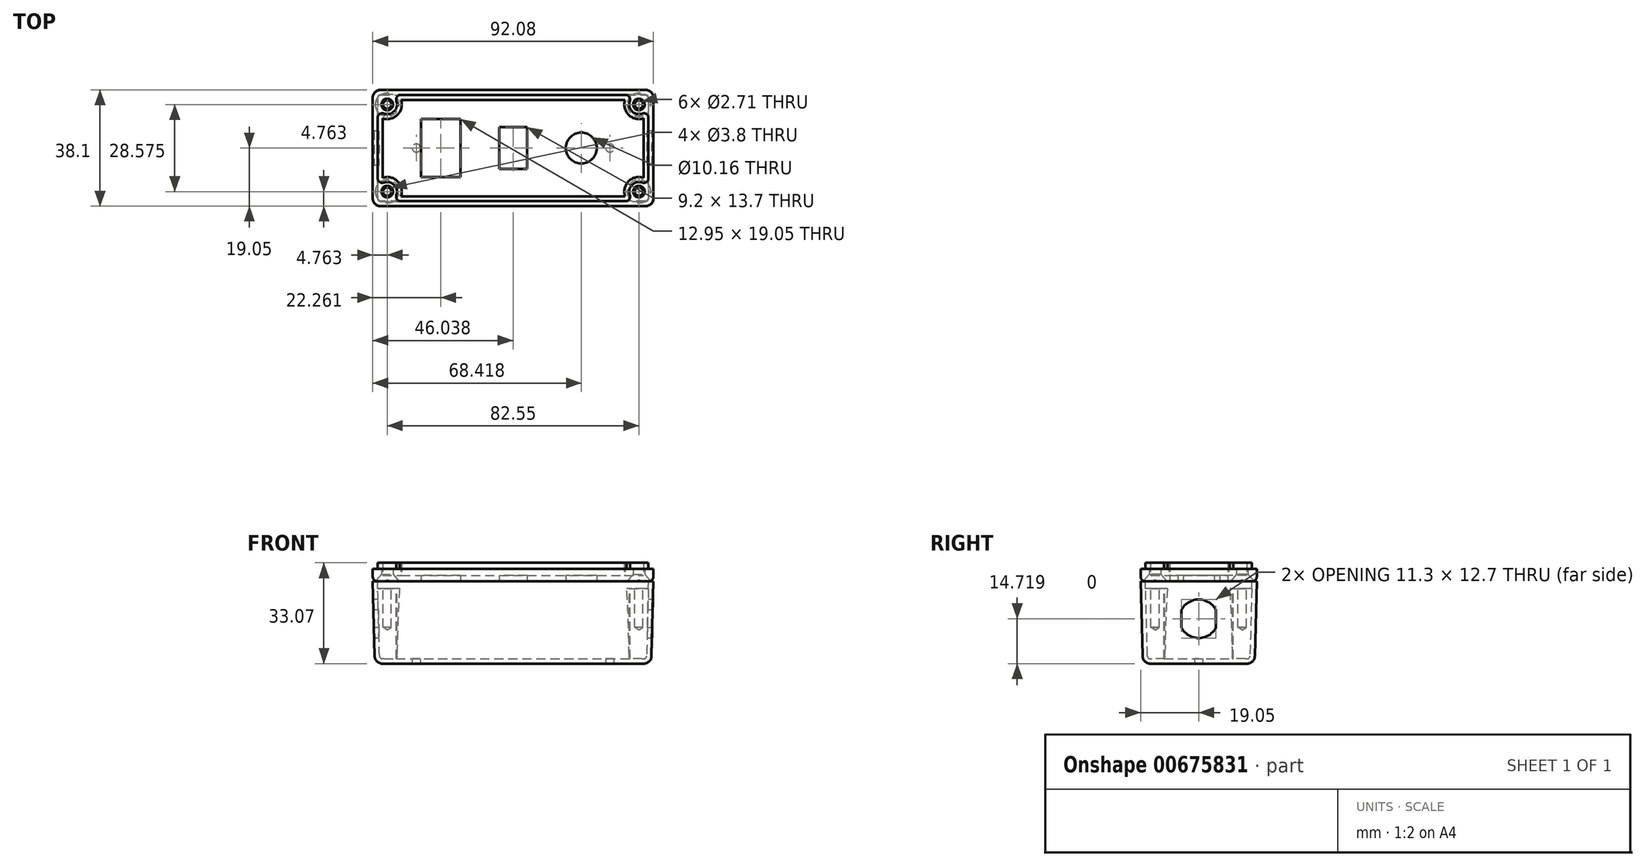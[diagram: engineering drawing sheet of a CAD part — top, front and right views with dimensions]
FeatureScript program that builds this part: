
annotation { "Feature Type Name" : "Feature", "Feature Type Description" : "" }
export const myFeature = defineFeature(function(context is Context, id is Id, definition is map)
    precondition{}
    {
        {
            var Q0;
            Q0=qCreatedBy(makeId("Top.planeOp"),FACE);
            var sketch = newSketch(context, id + "F0", { "sketchPlane" : qUnion([Q0])});
            skLineSegment(sketch, "E0.bottom", {"start": v(0, 0) * mm, "end": v(92.07, 0) * mm});
            skLineSegment(sketch, "E0.top", {"start": v(0, 38.1) * mm, "end": v(92.07, 38.1) * mm});
            skLineSegment(sketch, "E0.left", {"start": v(0, 0) * mm, "end": v(0, 38.1) * mm});
            skLineSegment(sketch, "E0.right", {"start": v(92.07, 0) * mm, "end": v(92.07, 38.1) * mm});
            skSolve(sketch);
        }
        {
            var Q0;
            Q0 = qSketchRegion(id + "F0", true);
            extrude(context, id + "F1", {"entities" : qUnion([Q0]), "oppositeDirection" : true, "depth" : 26.97 * mm, "offsetDistance" : 25.4 * mm, "hasDraft" : true, "draftAngle" : 1.5 * degree, "draftPullDirection" : true});
        }
        {
            var Q0;
            Q0=makeQuery(id+"F1.opExtrude","SWEPT_EDGE",EDGE,{"disambiguationData":[OSD([sQuery(id+"F0.wireOp",EDGE,"E0.bottom"),sQuery(id+"F0.wireOp",EDGE,"E0.right")])]});
            var Q1;
            Q1=makeQuery(id+"F1.opExtrude","CAP_EDGE",EDGE,{"disambiguationData":[OSD([sQuery(id+"F0.wireOp",EDGE,"E0.bottom")])],"isStart":false});
            var Q2;
            Q2=makeQuery(id+"F1.opExtrude","SWEPT_EDGE",EDGE,{"disambiguationData":[OSD([sQuery(id+"F0.wireOp",EDGE,"E0.bottom"),sQuery(id+"F0.wireOp",EDGE,"E0.left")])]});
            var Q3;
            Q3=makeQuery(id+"F1.opExtrude","SWEPT_EDGE",EDGE,{"disambiguationData":[OSD([sQuery(id+"F0.wireOp",EDGE,"E0.top"),sQuery(id+"F0.wireOp",EDGE,"E0.left")])]});
            var Q4;
            Q4=makeQuery(id+"F1.opExtrude","CAP_EDGE",EDGE,{"disambiguationData":[OSD([sQuery(id+"F0.wireOp",EDGE,"E0.left")])],"isStart":false});
            var Q5;
            Q5=makeQuery(id+"F1.opExtrude","CAP_EDGE",EDGE,{"disambiguationData":[OSD([sQuery(id+"F0.wireOp",EDGE,"E0.right")])],"isStart":false});
            var Q6;
            Q6=makeQuery(id+"F1.opExtrude","SWEPT_EDGE",EDGE,{"disambiguationData":[OSD([sQuery(id+"F0.wireOp",EDGE,"E0.top"),sQuery(id+"F0.wireOp",EDGE,"E0.right")])]});
            var Q7;
            Q7=makeQuery(id+"F1.opExtrude","CAP_EDGE",EDGE,{"disambiguationData":[OSD([sQuery(id+"F0.wireOp",EDGE,"E0.top")])],"isStart":false});
            fillet(context, id + "F2", {"entities" : qUnion([Q0, Q1, Q2, Q3, Q4, Q5, Q6, Q7]), "radius" : 2.54 * mm, "tangentPropagation" : true, "allowEdgeOverflow" : false});
        }
        {
            var Q0;
            Q0=makeQuery(id+"F1.opExtrude","CAP_FACE",FACE,{"disambiguationData":[OSD([sQuery(id+"F0.wireOp",EDGE,"E0.bottom"),sQuery(id+"F0.wireOp",EDGE,"E0.top"),sQuery(id+"F0.wireOp",EDGE,"E0.left"),sQuery(id+"F0.wireOp",EDGE,"E0.right")])],"isStart":true});
            shell(context, id + "F3", {"entities" : qUnion([Q0]), "thickness" : 1.57 * mm});
        }
        {
            var Q0;
            Q0=makeQuery(id+"F1.opExtrude","CAP_FACE",FACE,{"disambiguationData":[OSD([sQuery(id+"F0.wireOp",EDGE,"E0.bottom"),sQuery(id+"F0.wireOp",EDGE,"E0.top"),sQuery(id+"F0.wireOp",EDGE,"E0.left"),sQuery(id+"F0.wireOp",EDGE,"E0.right")])],"isStart":true});
            cPlane(context, id + "F4", {"entities" : qUnion([Q0]), "cplaneType" : CPlaneType.OFFSET, "offset" : 2.4 * mm, "oppositeDirection" : true, "width" : 152.4 * mm, "height" : 152.4 * mm});
        }
        {
            var Q0;
            Q0=qCreatedBy(id+"F4.planeOp",FACE);
            var sketch = newSketch(context, id + "F5", { "sketchPlane" : qUnion([Q0])});
            skArc(sketch, "E1", {"start": v(3.68, 30.35) * mm, "mid": v(7, 31.1) * mm, "end": v(7.75, 34.42) * mm});
            skLineSegment(sketch, "E2", {"start": v(46.04, 38.1) * mm, "end": v(46.04, 0) * mm, "construction": true});
            skLineSegment(sketch, "E3", {"start": v(0, 19.05) * mm, "end": v(92.08, 19.05) * mm, "construction": true});
            skPoint(sketch, "E3.endSnap0", {"position": v(46.04, 19.05) * mm});
            skArc(sketch, "E4", {"start": v(9.23, 36.52) * mm, "mid": v(7.94, 35.85) * mm, "end": v(7.75, 34.42) * mm});
            skArc(sketch, "E5", {"start": v(3.68, 30.35) * mm, "mid": v(2.25, 30.16) * mm, "end": v(1.58, 28.87) * mm});
            skLineSegment(sketch, "E6", {"start": v(1.58, 28.87) * mm, "end": v(1.58, 36.52) * mm});
            skLineSegment(sketch, "E7", {"start": v(1.58, 36.52) * mm, "end": v(9.23, 36.52) * mm});
            skPoint(sketch, "E8", {"position": v(4.76, 4.76) * mm});
            skPoint(sketch, "E9", {"position": v(87.31, 4.76) * mm});
            skPoint(sketch, "E10", {"position": v(87.31, 33.34) * mm});
            skLineSegment(sketch, "E11.MirrorCS", {"start": v(90.5, 36.52) * mm, "end": v(82.84, 36.52) * mm});
            skArc(sketch, "E12.MirrorCS", {"start": v(82.84, 36.52) * mm, "mid": v(84.13, 35.85) * mm, "end": v(84.33, 34.42) * mm});
            skArc(sketch, "E13.MirrorCS", {"start": v(88.4, 30.35) * mm, "mid": v(85.07, 31.1) * mm, "end": v(84.33, 34.42) * mm});
            skArc(sketch, "E14.MirrorCS", {"start": v(88.4, 30.35) * mm, "mid": v(89.83, 30.16) * mm, "end": v(90.5, 28.87) * mm});
            skLineSegment(sketch, "E15.MirrorCS", {"start": v(90.5, 28.87) * mm, "end": v(90.5, 36.52) * mm});
            skArc(sketch, "E16.MirrorCS", {"start": v(3.68, 7.75) * mm, "mid": v(7, 7) * mm, "end": v(7.75, 3.68) * mm});
            skArc(sketch, "E17.MirrorCS", {"start": v(3.68, 7.75) * mm, "mid": v(2.25, 7.94) * mm, "end": v(1.58, 9.23) * mm});
            skLineSegment(sketch, "E18.MirrorCS", {"start": v(1.58, 9.23) * mm, "end": v(1.58, 1.58) * mm});
            skLineSegment(sketch, "E19.MirrorCS", {"start": v(1.58, 1.58) * mm, "end": v(9.23, 1.58) * mm});
            skArc(sketch, "E20.MirrorCS", {"start": v(9.23, 1.58) * mm, "mid": v(7.94, 2.25) * mm, "end": v(7.75, 3.68) * mm});
            skLineSegment(sketch, "E21.MirrorCS", {"start": v(90.5, 9.23) * mm, "end": v(90.5, 1.58) * mm});
            skArc(sketch, "E22.MirrorCS", {"start": v(88.4, 7.75) * mm, "mid": v(89.83, 7.94) * mm, "end": v(90.5, 9.23) * mm});
            skArc(sketch, "E23.MirrorCS", {"start": v(88.4, 7.75) * mm, "mid": v(85.07, 7) * mm, "end": v(84.33, 3.68) * mm});
            skArc(sketch, "E24.MirrorCS", {"start": v(82.84, 1.58) * mm, "mid": v(84.13, 2.25) * mm, "end": v(84.33, 3.68) * mm});
            skLineSegment(sketch, "E25.MirrorCS", {"start": v(90.5, 1.58) * mm, "end": v(82.84, 1.58) * mm});
            skSolve(sketch);
        }
        {
            var Q0;
            Q0 = qSketchRegion(id + "F5", true);
            var Q1;
            Q1=makeQuery(id+"F3.opShell","OFFSET_FACE",FACE,{"disambiguationData":[OSD([sQuery(id+"F0.wireOp",EDGE,"E0.bottom"),sQuery(id+"F0.wireOp",EDGE,"E0.top"),sQuery(id+"F0.wireOp",EDGE,"E0.left"),sQuery(id+"F0.wireOp",EDGE,"E0.right")])]});
            extrude(context, id + "F6", {"entities" : qUnion([Q0]), "operationType" : NewBodyOperationType.ADD, "endBound" : BoundingType.UP_TO_SURFACE, "oppositeDirection" : true, "depth" : 25.4 * mm, "endBoundEntityFace" : qUnion([Q1]), "offsetDistance" : 25.4 * mm});
        }
        {
            var Q0;
            Q0=makeQuery(id+"F6.opExtrude","CAP_FACE",FACE,{"disambiguationData":[OSD([sQuery(id+"F5.wireOp",EDGE,"E1"),sQuery(id+"F5.wireOp",EDGE,"E4"),sQuery(id+"F5.wireOp",EDGE,"E5"),sQuery(id+"F5.wireOp",EDGE,"E6"),sQuery(id+"F5.wireOp",EDGE,"E7")])],"isStart":true});
            var sketch = newSketch(context, id + "F7", { "sketchPlane" : qUnion([Q0])});
            skPoint(sketch, "E26", {"position": v(4.76, 33.34) * mm});
            skPoint(sketch, "E27", {"position": v(4.76, 4.76) * mm});
            skPoint(sketch, "E28", {"position": v(87.31, 4.76) * mm});
            skPoint(sketch, "E29", {"position": v(87.31, 33.34) * mm});
            skSolve(sketch);
        }
        {
            var Q0;
            Q0=sQuery(id+"F7.wireOp",VERTEX,"E26");
            var Q1;
            Q1=sQuery(id+"F7.wireOp",VERTEX,"E27");
            var Q2;
            Q2=sQuery(id+"F7.wireOp",VERTEX,"E28");
            var Q3;
            Q3=sQuery(id+"F7.wireOp",VERTEX,"E29");
            var Q4;
            Q4=makeQuery(id+"F1.opExtrude","SWEPT_BODY",BODY,{"disambiguationData":[OSD([sQuery(id+"F0.wireOp",EDGE,"E0.bottom"),sQuery(id+"F0.wireOp",EDGE,"E0.top"),sQuery(id+"F0.wireOp",EDGE,"E0.left"),sQuery(id+"F0.wireOp",EDGE,"E0.right")])]});
            hole(context, id + "F8", {"style" : HoleStyle.SIMPLE, "endStyle" : HoleEndStyle.BLIND, "standardTappedOrClearance" : lookupTablePath({ "standard" : "ANSI", "engagement" : "75%", "pitch" : "32 tpi", "size" : "#6", "type" : "Tapped" }), "standardBlindInLast" : lookupTablePath({ "standard" : "ANSI", "engagement" : "75%", "pitch" : "32 tpi", "size" : "#6", "type" : "Tapped" }), "holeDiameter" : 2.7 * mm, "majorDiameter" : 3.5 * mm, "showTappedDepth" : true, "holeDepth" : 12.7 * mm, "isTappedThrough" : true, "tappedDepth" : 10.32 * mm, "tapClearance" : 3, "startFromSketch" : true, "locations" : qUnion([Q0, Q1, Q2, Q3]), "scope" : qUnion([Q4])});
        }
        {
            var Q0;
            Q0=qCreatedBy(makeId("Top.planeOp"),FACE);
            var sketch = newSketch(context, id + "F9", { "sketchPlane" : qUnion([Q0])});
            skLineSegment(sketch, "E30.bottom", {"start": v(2.54, 0) * mm, "end": v(89.53, 0) * mm});
            skLineSegment(sketch, "E30.top", {"start": v(2.54, 38.1) * mm, "end": v(89.53, 38.1) * mm});
            skLineSegment(sketch, "E30.left", {"start": v(0, 2.54) * mm, "end": v(0, 35.56) * mm});
            skLineSegment(sketch, "E30.right", {"start": v(92.08, 2.54) * mm, "end": v(92.08, 35.56) * mm});
            skPoint(sketch, "E31.visualSharp", {"position": v(0, 38.1) * mm});
            skArc(sketch, "E31.filletArc", {"start": v(2.54, 38.1) * mm, "mid": v(0.74, 37.36) * mm, "end": v(0, 35.56) * mm});
            skPoint(sketch, "E32.visualSharp", {"position": v(92.08, 38.1) * mm});
            skArc(sketch, "E32.filletArc", {"start": v(92.08, 35.56) * mm, "mid": v(91.33, 37.36) * mm, "end": v(89.53, 38.1) * mm});
            skPoint(sketch, "E33.visualSharp", {"position": v(92.08, 0) * mm});
            skArc(sketch, "E33.filletArc", {"start": v(89.53, 0) * mm, "mid": v(91.33, 0.74) * mm, "end": v(92.08, 2.54) * mm});
            skPoint(sketch, "E34.visualSharp", {"position": v(0, 0) * mm});
            skArc(sketch, "E34.filletArc", {"start": v(0, 2.54) * mm, "mid": v(0.74, 0.74) * mm, "end": v(2.54, 0) * mm});
            skSolve(sketch);
        }
        {
            var Q0;
            Q0 = qSketchRegion(id + "F9", true);
            extrude(context, id + "F10", {"entities" : qUnion([Q0]), "depth" : 4.06 * mm, "offsetDistance" : 25.4 * mm});
        }
        {
            var Q0;
            Q0=qCreatedBy(id+"F4.planeOp",FACE);
            var sketch = newSketch(context, id + "F11", { "sketchPlane" : qUnion([Q0])});
            skArc(sketch, "E35.0", {"start": v(3.68, 30.35) * mm, "mid": v(7, 31.1) * mm, "end": v(7.75, 34.42) * mm});
            skArc(sketch, "E35.1", {"start": v(8.8, 36.46) * mm, "mid": v(7.83, 35.66) * mm, "end": v(7.75, 34.42) * mm});
            skArc(sketch, "E35.2", {"start": v(3.68, 30.35) * mm, "mid": v(2.44, 30.27) * mm, "end": v(1.64, 29.3) * mm});
            skArc(sketch, "E36.0", {"start": v(8.8, 1.64) * mm, "mid": v(7.83, 2.44) * mm, "end": v(7.75, 3.68) * mm});
            skArc(sketch, "E36.1", {"start": v(3.68, 7.75) * mm, "mid": v(7, 7) * mm, "end": v(7.75, 3.68) * mm});
            skArc(sketch, "E36.2", {"start": v(3.68, 7.75) * mm, "mid": v(2.44, 7.83) * mm, "end": v(1.64, 8.8) * mm});
            skArc(sketch, "E37.0", {"start": v(83.28, 1.64) * mm, "mid": v(84.25, 2.44) * mm, "end": v(84.33, 3.68) * mm});
            skArc(sketch, "E37.1", {"start": v(88.4, 7.75) * mm, "mid": v(85.07, 7) * mm, "end": v(84.33, 3.68) * mm});
            skArc(sketch, "E37.2", {"start": v(88.4, 7.75) * mm, "mid": v(89.64, 7.83) * mm, "end": v(90.44, 8.8) * mm});
            skArc(sketch, "E38.0", {"start": v(88.4, 30.35) * mm, "mid": v(89.64, 30.27) * mm, "end": v(90.44, 29.3) * mm});
            skArc(sketch, "E38.1", {"start": v(88.4, 30.35) * mm, "mid": v(85.07, 31.1) * mm, "end": v(84.33, 34.42) * mm});
            skArc(sketch, "E38.2", {"start": v(83.28, 36.46) * mm, "mid": v(84.25, 35.66) * mm, "end": v(84.33, 34.42) * mm});
            skLineSegment(sketch, "E39", {"start": v(8.8, 36.46) * mm, "end": v(83.28, 36.46) * mm});
            skLineSegment(sketch, "E40", {"start": v(90.44, 29.3) * mm, "end": v(90.44, 8.8) * mm});
            skLineSegment(sketch, "E41", {"start": v(83.28, 1.64) * mm, "end": v(8.8, 1.64) * mm});
            skLineSegment(sketch, "E42", {"start": v(1.64, 8.8) * mm, "end": v(1.64, 29.3) * mm});
            skSolve(sketch);
        }
        {
            var Q0;
            Q0=makeQuery(id+"F10.opExtrude","CAP_FACE",FACE,{"disambiguationData":[OSD([sQuery(id+"F9.wireOp",EDGE,"E30.bottom"),sQuery(id+"F9.wireOp",EDGE,"E30.top"),sQuery(id+"F9.wireOp",EDGE,"E30.left"),sQuery(id+"F9.wireOp",EDGE,"E30.right"),sQuery(id+"F9.wireOp",EDGE,"E31.filletArc"),sQuery(id+"F9.wireOp",EDGE,"E32.filletArc"),sQuery(id+"F9.wireOp",EDGE,"E33.filletArc"),sQuery(id+"F9.wireOp",EDGE,"E34.filletArc")])],"isStart":false});
            var sketch = newSketch(context, id + "F12", { "sketchPlane" : qUnion([Q0])});
            skLineSegment(sketch, "E43.0", {"start": v(1.64, 8.8) * mm, "end": v(1.64, 29.3) * mm});
            skArc(sketch, "E43.1", {"start": v(3.68, 7.75) * mm, "mid": v(7, 7) * mm, "end": v(7.75, 3.68) * mm});
            skArc(sketch, "E43.2", {"start": v(3.68, 7.75) * mm, "mid": v(2.44, 7.83) * mm, "end": v(1.64, 8.8) * mm});
            skArc(sketch, "E43.3", {"start": v(8.8, 1.64) * mm, "mid": v(7.83, 2.44) * mm, "end": v(7.75, 3.68) * mm});
            skLineSegment(sketch, "E43.4", {"start": v(83.28, 1.64) * mm, "end": v(8.8, 1.64) * mm});
            skArc(sketch, "E43.5", {"start": v(3.68, 30.35) * mm, "mid": v(2.44, 30.27) * mm, "end": v(1.64, 29.3) * mm});
            skArc(sketch, "E43.6", {"start": v(3.68, 30.35) * mm, "mid": v(7, 31.1) * mm, "end": v(7.75, 34.42) * mm});
            skArc(sketch, "E43.7", {"start": v(8.8, 36.46) * mm, "mid": v(7.83, 35.66) * mm, "end": v(7.75, 34.42) * mm});
            skLineSegment(sketch, "E43.8", {"start": v(8.8, 36.46) * mm, "end": v(83.28, 36.46) * mm});
            skArc(sketch, "E43.9", {"start": v(83.28, 36.46) * mm, "mid": v(84.25, 35.66) * mm, "end": v(84.33, 34.42) * mm});
            skArc(sketch, "E43.10", {"start": v(88.4, 30.35) * mm, "mid": v(85.07, 31.1) * mm, "end": v(84.33, 34.42) * mm});
            skArc(sketch, "E43.11", {"start": v(88.4, 30.35) * mm, "mid": v(89.64, 30.27) * mm, "end": v(90.44, 29.3) * mm});
            skLineSegment(sketch, "E43.12", {"start": v(90.44, 29.3) * mm, "end": v(90.44, 8.8) * mm});
            skArc(sketch, "E43.13", {"start": v(88.4, 7.75) * mm, "mid": v(89.64, 7.83) * mm, "end": v(90.44, 8.8) * mm});
            skArc(sketch, "E43.14", {"start": v(88.4, 7.75) * mm, "mid": v(85.07, 7) * mm, "end": v(84.33, 3.68) * mm});
            skArc(sketch, "E43.15", {"start": v(83.28, 1.64) * mm, "mid": v(84.25, 2.44) * mm, "end": v(84.33, 3.68) * mm});
            skLineSegment(sketch, "E44.0", {"start": v(88.84, 28.81) * mm, "end": v(88.84, 9.29) * mm});
            skArc(sketch, "E44.1", {"start": v(88.84, 28.81) * mm, "mid": v(83.94, 29.96) * mm, "end": v(82.79, 34.86) * mm});
            skArc(sketch, "E44.2", {"start": v(88.84, 9.29) * mm, "mid": v(83.94, 8.14) * mm, "end": v(82.79, 3.24) * mm});
            skLineSegment(sketch, "E44.3", {"start": v(9.29, 34.86) * mm, "end": v(82.79, 34.86) * mm});
            skLineSegment(sketch, "E44.4", {"start": v(82.79, 3.24) * mm, "end": v(9.29, 3.24) * mm});
            skArc(sketch, "E44.5", {"start": v(3.24, 9.29) * mm, "mid": v(8.14, 8.14) * mm, "end": v(9.29, 3.24) * mm});
            skLineSegment(sketch, "E44.6", {"start": v(3.24, 9.29) * mm, "end": v(3.24, 28.81) * mm});
            skArc(sketch, "E44.7", {"start": v(3.24, 28.81) * mm, "mid": v(8.14, 29.96) * mm, "end": v(9.29, 34.86) * mm});
            skSolve(sketch);
        }
        {
            var Q0;
            Q0 = qSketchRegion(id + "F12", true);
            extrude(context, id + "F13", {"entities" : qUnion([Q0]), "operationType" : NewBodyOperationType.ADD, "depth" : 2.03 * mm, "offsetDistance" : 25.4 * mm});
        }
        {
            var Q0;
            Q0=makeQuery(id+"F13.boolean.opBoolean","SPLIT",FACE,{"disambiguationData":[TD([makeQuery(id+"F13.opExtrude","SWEPT_FACE",FACE,{"disambiguationData":[OSD([sQuery(id+"F12.wireOp",EDGE,"E44.0")])]})])],"derivedFrom":makeQuery(id+"F10.opExtrude","CAP_FACE",FACE,{"disambiguationData":[OSD([sQuery(id+"F9.wireOp",EDGE,"E30.bottom"),sQuery(id+"F9.wireOp",EDGE,"E30.top"),sQuery(id+"F9.wireOp",EDGE,"E30.left"),sQuery(id+"F9.wireOp",EDGE,"E30.right"),sQuery(id+"F9.wireOp",EDGE,"E31.filletArc"),sQuery(id+"F9.wireOp",EDGE,"E32.filletArc"),sQuery(id+"F9.wireOp",EDGE,"E33.filletArc"),sQuery(id+"F9.wireOp",EDGE,"E34.filletArc")])],"isStart":false})});
            var sketch = newSketch(context, id + "F14", { "sketchPlane" : qUnion([Q0])});
            skArc(sketch, "E45.0", {"start": v(3.24, 28.81) * mm, "mid": v(8.14, 29.96) * mm, "end": v(9.29, 34.86) * mm});
            skLineSegment(sketch, "E45.1", {"start": v(9.29, 34.86) * mm, "end": v(82.79, 34.86) * mm});
            skLineSegment(sketch, "E45.2", {"start": v(3.24, 9.29) * mm, "end": v(3.24, 28.81) * mm});
            skArc(sketch, "E45.3", {"start": v(3.24, 9.29) * mm, "mid": v(8.14, 8.14) * mm, "end": v(9.29, 3.24) * mm});
            skLineSegment(sketch, "E45.4", {"start": v(82.79, 3.24) * mm, "end": v(9.29, 3.24) * mm});
            skArc(sketch, "E45.5", {"start": v(88.84, 28.81) * mm, "mid": v(83.94, 29.96) * mm, "end": v(82.79, 34.86) * mm});
            skLineSegment(sketch, "E45.6", {"start": v(88.84, 28.81) * mm, "end": v(88.84, 9.29) * mm});
            skArc(sketch, "E45.7", {"start": v(88.84, 9.29) * mm, "mid": v(83.94, 8.14) * mm, "end": v(82.79, 3.24) * mm});
            skSolve(sketch);
        }
        {
            var Q0;
            Q0 = qSketchRegion(id + "F14", true);
            extrude(context, id + "F15", {"entities" : qUnion([Q0]), "operationType" : NewBodyOperationType.REMOVE, "oppositeDirection" : true, "depth" : 2.08 * mm, "offsetDistance" : 25.4 * mm});
        }
        {
            var Q0;
            Q0=makeQuery(id+"F10.opExtrude","CAP_FACE",FACE,{"disambiguationData":[OSD([sQuery(id+"F9.wireOp",EDGE,"E30.bottom"),sQuery(id+"F9.wireOp",EDGE,"E30.top"),sQuery(id+"F9.wireOp",EDGE,"E30.left"),sQuery(id+"F9.wireOp",EDGE,"E30.right"),sQuery(id+"F9.wireOp",EDGE,"E31.filletArc"),sQuery(id+"F9.wireOp",EDGE,"E32.filletArc"),sQuery(id+"F9.wireOp",EDGE,"E33.filletArc"),sQuery(id+"F9.wireOp",EDGE,"E34.filletArc")])],"isStart":true});
            var sketch = newSketch(context, id + "F16", { "sketchPlane" : qUnion([Q0])});
            skPoint(sketch, "E46", {"position": v(4.76, -4.76) * mm});
            skPoint(sketch, "E47", {"position": v(87.31, -4.76) * mm});
            skPoint(sketch, "E48", {"position": v(87.31, -33.34) * mm});
            skPoint(sketch, "E49", {"position": v(4.76, -33.34) * mm});
            skLineSegment(sketch, "E50", {"start": v(46.04, 0) * mm, "end": v(46.04, -38.1) * mm, "construction": true});
            skLineSegment(sketch, "E51", {"start": v(92.08, -19.05) * mm, "end": v(0, -19.05) * mm, "construction": true});
            skSolve(sketch);
        }
        {
            var Q0;
            Q0=sQuery(id+"F16.wireOp",VERTEX,"E46");
            var Q1;
            Q1=sQuery(id+"F16.wireOp",VERTEX,"E49");
            var Q2;
            Q2=sQuery(id+"F16.wireOp",VERTEX,"E47");
            var Q3;
            Q3=sQuery(id+"F16.wireOp",VERTEX,"E48");
            var Q4;
            Q4=makeQuery(id+"F10.opExtrude","SWEPT_BODY",BODY,{"disambiguationData":[OSD([sQuery(id+"F9.wireOp",EDGE,"E30.bottom"),sQuery(id+"F9.wireOp",EDGE,"E30.top"),sQuery(id+"F9.wireOp",EDGE,"E30.left"),sQuery(id+"F9.wireOp",EDGE,"E30.right"),sQuery(id+"F9.wireOp",EDGE,"E31.filletArc"),sQuery(id+"F9.wireOp",EDGE,"E32.filletArc"),sQuery(id+"F9.wireOp",EDGE,"E33.filletArc"),sQuery(id+"F9.wireOp",EDGE,"E34.filletArc")])]});
            hole(context, id + "F17", {"style" : HoleStyle.C_SINK, "endStyle" : HoleEndStyle.THROUGH, "standardTappedOrClearance" : lookupTablePath({ "standard" : "ANSI", "fit" : "Normal (ASME)", "size" : "#6", "type" : "Clearance" }), "standardBlindInLast" : lookupTablePath({ "fit" : "Free", "standard" : "ANSI", "size" : "#6", "type" : "Clearance" }), "holeDiameter" : 3.8 * mm, "cSinkDiameter" : 7.8 * mm, "cSinkAngle" : 82 * degree, "majorDiameter" : 3.5 * mm, "isTappedThrough" : true, "tappedDepth" : 2.4 * mm, "tapClearance" : 3, "startFromSketch" : true, "locations" : qUnion([Q0, Q1, Q2, Q3]), "scope" : qUnion([Q4])});
        }
        {
            var Q0;
            Q0=makeQuery(id+"F10.opExtrude","CAP_EDGE",EDGE,{"disambiguationData":[OSD([sQuery(id+"F9.wireOp",EDGE,"E30.bottom")])],"isStart":true});
            var Q1;
            Q1=makeQuery(id+"F10.opExtrude","CAP_EDGE",EDGE,{"disambiguationData":[OSD([sQuery(id+"F9.wireOp",EDGE,"E30.right")])],"isStart":true});
            var Q2;
            Q2=makeQuery(id+"F10.opExtrude","CAP_EDGE",EDGE,{"disambiguationData":[OSD([sQuery(id+"F9.wireOp",EDGE,"E30.top")])],"isStart":true});
            var Q3;
            Q3=makeQuery(id+"F10.opExtrude","CAP_EDGE",EDGE,{"disambiguationData":[OSD([sQuery(id+"F9.wireOp",EDGE,"E30.left")])],"isStart":true});
            fillet(context, id + "F18", {"entities" : qUnion([Q0, Q1, Q2, Q3]), "radius" : 1.57 * mm, "tangentPropagation" : true, "allowEdgeOverflow" : false});
        }
        {
            var Q0;
            Q0=makeQuery(id+"F18.opFillet","SPLIT",FACE,{"disambiguationData":[OD(4.0)],"derivedFrom":makeQuery(id+"F10.opExtrude","CAP_FACE",FACE,{"disambiguationData":[OSD([sQuery(id+"F9.wireOp",EDGE,"E30.bottom"),sQuery(id+"F9.wireOp",EDGE,"E30.top"),sQuery(id+"F9.wireOp",EDGE,"E30.left"),sQuery(id+"F9.wireOp",EDGE,"E30.right"),sQuery(id+"F9.wireOp",EDGE,"E31.filletArc"),sQuery(id+"F9.wireOp",EDGE,"E32.filletArc"),sQuery(id+"F9.wireOp",EDGE,"E33.filletArc"),sQuery(id+"F9.wireOp",EDGE,"E34.filletArc")])],"isStart":true})});
            var sketch = newSketch(context, id + "F19", { "sketchPlane" : qUnion([Q0])});
            skLineSegment(sketch, "E52.bottom", {"start": v(15.78, -9.52) * mm, "end": v(28.74, -9.52) * mm});
            skLineSegment(sketch, "E52.top", {"start": v(15.78, -28.57) * mm, "end": v(28.74, -28.57) * mm});
            skLineSegment(sketch, "E52.left", {"start": v(15.78, -9.52) * mm, "end": v(15.78, -28.57) * mm});
            skLineSegment(sketch, "E52.right", {"start": v(28.74, -9.52) * mm, "end": v(28.74, -28.57) * mm});
            skLineSegment(sketch, "E53", {"start": v(1.57, -19.05) * mm, "end": v(90.5, -19.05) * mm, "construction": true});
            skPoint(sketch, "E54", {"position": v(15.78, -19.05) * mm});
            skCircle(sketch, "E55", {"center": v(68.42, -19.05) * mm, "radius": 5.08 * mm});
            skCircle(sketch, "E56", {"center": v(68.42, -19.05) * mm, "radius": 11.18 * mm, "construction": true});
            skLineSegment(sketch, "E57.bottom", {"start": v(14.96, -8.7) * mm, "end": v(29.56, -8.7) * mm, "construction": true});
            skLineSegment(sketch, "E57.top", {"start": v(14.96, -29.4) * mm, "end": v(29.56, -29.4) * mm, "construction": true});
            skLineSegment(sketch, "E57.left", {"start": v(14.96, -8.7) * mm, "end": v(14.96, -29.4) * mm, "construction": true});
            skLineSegment(sketch, "E57.right", {"start": v(29.56, -8.7) * mm, "end": v(29.56, -29.4) * mm, "construction": true});
            skPoint(sketch, "E58", {"position": v(14.96, -19.05) * mm});
            skLineSegment(sketch, "E59", {"start": v(22.26, -9.52) * mm, "end": v(22.26, -8.7) * mm, "construction": true});
            skLineSegment(sketch, "E60.bottom", {"start": v(41.44, -12.2) * mm, "end": v(50.64, -12.2) * mm});
            skLineSegment(sketch, "E60.top", {"start": v(41.44, -25.9) * mm, "end": v(50.64, -25.9) * mm});
            skLineSegment(sketch, "E60.left", {"start": v(41.44, -12.2) * mm, "end": v(41.44, -25.9) * mm});
            skLineSegment(sketch, "E60.right", {"start": v(50.64, -12.2) * mm, "end": v(50.64, -25.9) * mm});
            skPoint(sketch, "E61", {"position": v(41.44, -19.05) * mm});
            skLineSegment(sketch, "E62", {"start": v(46.04, -12.2) * mm, "end": v(46.04, 0) * mm, "construction": true});
            skCircle(sketch, "E63", {"center": v(68.42, -19.05) * mm, "radius": 6.35 * mm, "construction": true});
            skSolve(sketch);
        }
        {
            var Q0;
            Q0 = qSketchRegion(id + "F19", true);
            extrude(context, id + "F20", {"entities" : qUnion([Q0]), "operationType" : NewBodyOperationType.REMOVE, "endBound" : BoundingType.THROUGH_ALL, "oppositeDirection" : true, "depth" : 25.4 * mm, "offsetDistance" : 25.4 * mm});
        }
        {
            var Q0;
            Q0=qCreatedBy(makeId("Right.planeOp"),FACE);
            var sketch = newSketch(context, id + "F21", { "sketchPlane" : qUnion([Q0])});
            skLineSegment(sketch, "E64", {"start": v(19.05, 0) * mm, "end": v(19.05, -24.5) * mm, "construction": true});
            skArc(sketch, "E65", {"start": v(24.7, -9.36) * mm, "mid": v(19.05, -5.9) * mm, "end": v(13.4, -9.36) * mm});
            skLineSegment(sketch, "E66", {"start": v(24.7, -9.36) * mm, "end": v(24.7, -15.15) * mm});
            skLineSegment(sketch, "E67", {"start": v(13.4, -9.36) * mm, "end": v(13.4, -15.15) * mm});
            skArc(sketch, "E68.trimOffspring", {"start": v(13.4, -15.15) * mm, "mid": v(19.05, -18.6) * mm, "end": v(24.7, -15.15) * mm});
            skSolve(sketch);
        }
        {
            var Q0;
            Q0 = qSketchRegion(id + "F21", true);
            extrude(context, id + "F22", {"entities" : qUnion([Q0]), "operationType" : NewBodyOperationType.REMOVE, "endBound" : BoundingType.THROUGH_ALL, "depth" : 25.4 * mm, "offsetDistance" : 25.4 * mm});
        }
        {
            var Q0;
            Q0=makeQuery(id+"F1.opExtrude","CAP_FACE",FACE,{"disambiguationData":[OSD([sQuery(id+"F0.wireOp",EDGE,"E0.bottom"),sQuery(id+"F0.wireOp",EDGE,"E0.top"),sQuery(id+"F0.wireOp",EDGE,"E0.left"),sQuery(id+"F0.wireOp",EDGE,"E0.right")])],"isStart":false});
            var sketch = newSketch(context, id + "F23", { "sketchPlane" : qUnion([Q0])});
            skPoint(sketch, "E69", {"position": v(14.29, -19.05) * mm});
            skPoint(sketch, "E70", {"position": v(77.79, -19.05) * mm});
            skLineSegment(sketch, "E71", {"start": v(3.18, -19.05) * mm, "end": v(88.9, -19.05) * mm, "construction": true});
            skLineSegment(sketch, "E72", {"start": v(46.04, -3.18) * mm, "end": v(46.04, -34.92) * mm, "construction": true});
            skSolve(sketch);
        }
        {
            var Q0;
            Q0=sQuery(id+"F23.wireOp",VERTEX,"E69");
            var Q1;
            Q1=sQuery(id+"F23.wireOp",VERTEX,"E70");
            var Q2;
            Q2=makeQuery(id+"F1.opExtrude","SWEPT_BODY",BODY,{"disambiguationData":[OSD([sQuery(id+"F0.wireOp",EDGE,"E0.bottom"),sQuery(id+"F0.wireOp",EDGE,"E0.top"),sQuery(id+"F0.wireOp",EDGE,"E0.left"),sQuery(id+"F0.wireOp",EDGE,"E0.right")])]});
            hole(context, id + "F24", {"style" : HoleStyle.SIMPLE, "endStyle" : HoleEndStyle.BLIND, "standardTappedOrClearance" : lookupTablePath({ "standard" : "ANSI", "engagement" : "75%", "pitch" : "32 tpi", "size" : "#6", "type" : "Tapped" }), "standardBlindInLast" : lookupTablePath({ "standard" : "ANSI", "engagement" : "75%", "pitch" : "32 tpi", "size" : "#6", "type" : "Tapped" }), "holeDiameter" : 2.7 * mm, "majorDiameter" : 3.5 * mm, "showTappedDepth" : true, "holeDepth" : 12.7 * mm, "isTappedThrough" : true, "tappedDepth" : 10.32 * mm, "tapClearance" : 3, "startFromSketch" : true, "locations" : qUnion([Q0, Q1]), "scope" : qUnion([Q2])});
        }
    });
